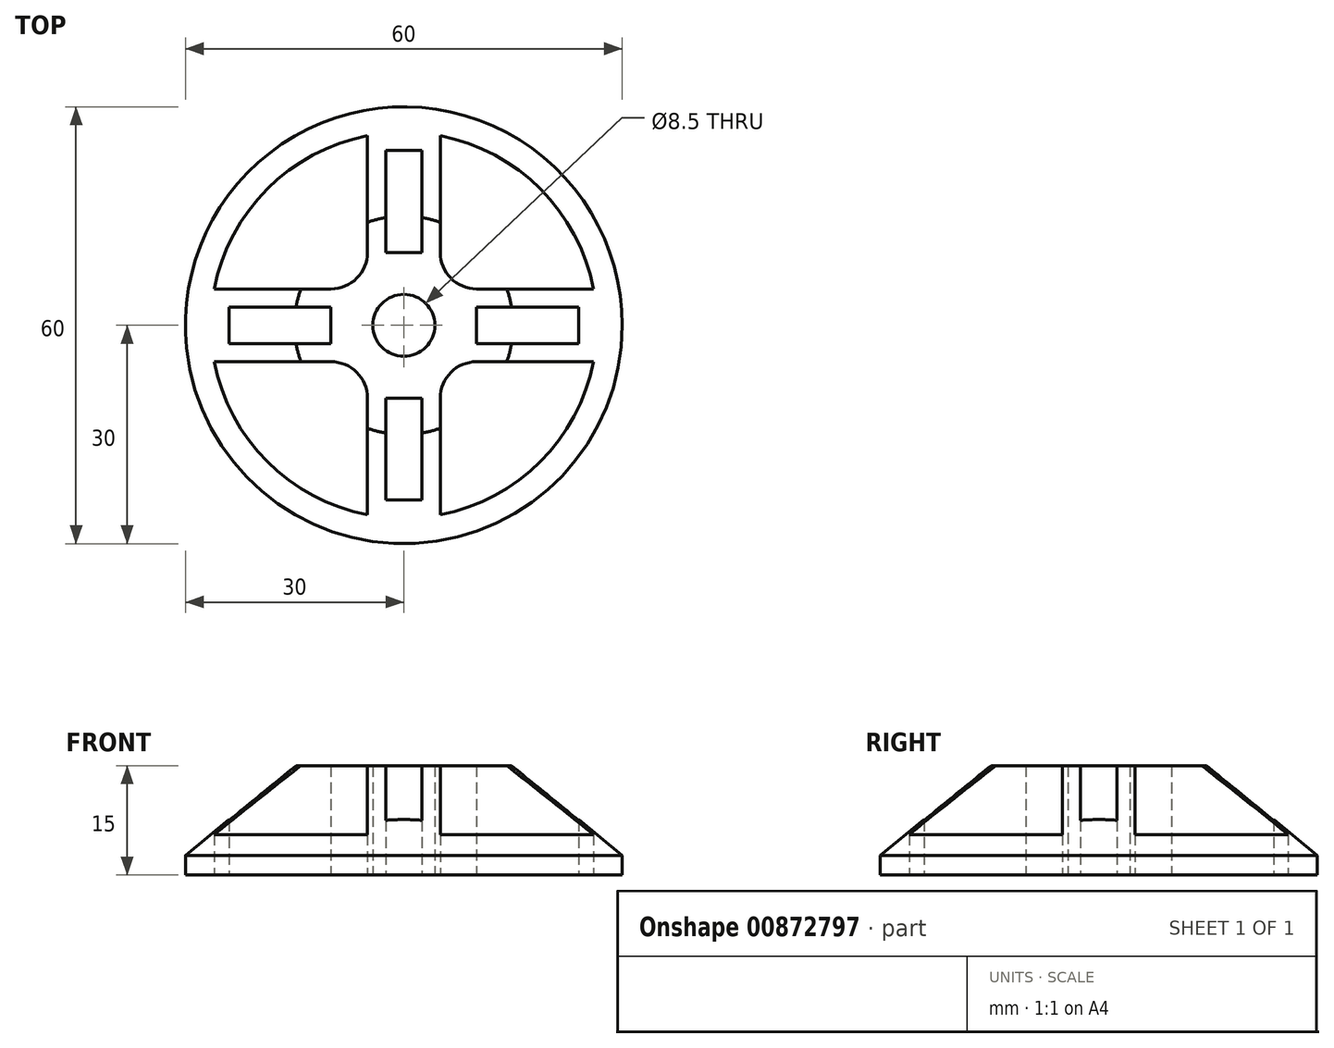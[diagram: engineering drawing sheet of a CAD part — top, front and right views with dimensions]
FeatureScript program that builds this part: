
annotation { "Feature Type Name" : "Feature", "Feature Type Description" : "" }
export const myFeature = defineFeature(function(context is Context, id is Id, definition is map)
    precondition{}
    {
        {
            assignVariable(context, id + "F0", {"name" : "Alto", "anyValue" : 15});
        }
        {
            var Q0;
            Q0=qCreatedBy(makeId("Top.planeOp"),FACE);
            var sketch = newSketch(context, id + "F1", { "sketchPlane" : qUnion([Q0])});
            skCircle(sketch, "E0", {"center": v(0, 0) * mm, "radius": 4.25 * mm});
            skCircle(sketch, "E1", {"center": v(0, 0) * mm, "radius": 30 * mm});
            skCircle(sketch, "E2", {"center": v(0, 0) * mm, "radius": 26.5 * mm});
            skLineSegment(sketch, "E3.bottom", {"start": v(-5, 42.51) * mm, "end": v(5, 42.51) * mm});
            skLineSegment(sketch, "E3.top", {"start": v(-5, -42.51) * mm, "end": v(5, -42.51) * mm});
            skLineSegment(sketch, "E3.left", {"start": v(-5, 42.51) * mm, "end": v(-5, -42.51) * mm});
            skLineSegment(sketch, "E3.right", {"start": v(5, 42.51) * mm, "end": v(5, -42.51) * mm});
            skLineSegment(sketch, "E4.bottom", {"start": v(-44.3, -5) * mm, "end": v(44.3, -5) * mm});
            skLineSegment(sketch, "E4.top", {"start": v(-44.3, 5) * mm, "end": v(44.3, 5) * mm});
            skLineSegment(sketch, "E4.left", {"start": v(-44.3, -5) * mm, "end": v(-44.3, 5) * mm});
            skLineSegment(sketch, "E4.right", {"start": v(44.3, -5) * mm, "end": v(44.3, 5) * mm});
            skLineSegment(sketch, "E5.bottom", {"start": v(10, -10) * mm, "end": v(-10, -10) * mm});
            skLineSegment(sketch, "E5.top", {"start": v(10, 10) * mm, "end": v(-10, 10) * mm});
            skLineSegment(sketch, "E5.left", {"start": v(10, -10) * mm, "end": v(10, 10) * mm});
            skLineSegment(sketch, "E5.right", {"start": v(-10, -10) * mm, "end": v(-10, 10) * mm});
            skLineSegment(sketch, "E6.bottom", {"start": v(24, -2.5) * mm, "end": v(-24, -2.5) * mm});
            skLineSegment(sketch, "E6.top", {"start": v(24, 2.5) * mm, "end": v(-24, 2.5) * mm});
            skLineSegment(sketch, "E6.left", {"start": v(24, -2.5) * mm, "end": v(24, 2.5) * mm});
            skLineSegment(sketch, "E6.right", {"start": v(-24, -2.5) * mm, "end": v(-24, 2.5) * mm});
            skLineSegment(sketch, "E7.bottom", {"start": v(-2.5, 24) * mm, "end": v(2.5, 24) * mm});
            skLineSegment(sketch, "E7.top", {"start": v(-2.5, -24) * mm, "end": v(2.5, -24) * mm});
            skLineSegment(sketch, "E7.left", {"start": v(-2.5, 24) * mm, "end": v(-2.5, -24) * mm});
            skLineSegment(sketch, "E7.right", {"start": v(2.5, 24) * mm, "end": v(2.5, -24) * mm});
            skSolve(sketch);
        }
        {
            var Q0;
            {var subQ0=sQuery(id+"F1.wireOp",EDGE,"E3.left");var subQ1=sQuery(id+"F1.wireOp",EDGE,"E1");var subQ2=makeQuery(id+"F1.imprint","INTERSECT",VERTEX,{"disambiguationData":[OD(0.0)],"derivedFrom":[subQ1,subQ0]});Q0=makeQuery(id+"F1.imprint","IMPRINT",FACE,{"disambiguationData":[TD([[makeQuery(id+"F1.imprint","IMPRINT",EDGE,{"disambiguationData":[TD([[subQ2,-1.0]])],"derivedFrom":subQ1}),1.0]])]});}
            var Q1;
            {var subQ0=sQuery(id+"F1.wireOp",EDGE,"E4.top");var subQ1=sQuery(id+"F1.wireOp",EDGE,"E1");var subQ2=makeQuery(id+"F1.imprint","INTERSECT",VERTEX,{"disambiguationData":[OD(1.0)],"derivedFrom":[subQ1,subQ0]});Q1=makeQuery(id+"F1.imprint","IMPRINT",FACE,{"disambiguationData":[TD([[makeQuery(id+"F1.imprint","IMPRINT",EDGE,{"disambiguationData":[TD([[subQ2,-1.0]])],"derivedFrom":subQ1}),1.0]])]});}
            var Q2;
            {var subQ0=sQuery(id+"F1.wireOp",EDGE,"E4.bottom");var subQ1=sQuery(id+"F1.wireOp",EDGE,"E1");var subQ2=makeQuery(id+"F1.imprint","INTERSECT",VERTEX,{"disambiguationData":[OD(0.0)],"derivedFrom":[subQ1,subQ0]});Q2=makeQuery(id+"F1.imprint","IMPRINT",FACE,{"disambiguationData":[TD([[makeQuery(id+"F1.imprint","IMPRINT",EDGE,{"disambiguationData":[TD([[subQ2,-1.0]])],"derivedFrom":subQ1}),1.0]])]});}
            var Q3;
            {var subQ0=sQuery(id+"F1.wireOp",EDGE,"E4.top");var subQ1=sQuery(id+"F1.wireOp",EDGE,"E2");var subQ2=makeQuery(id+"F1.imprint","INTERSECT",VERTEX,{"disambiguationData":[OD(1.0)],"derivedFrom":[subQ1,subQ0]});Q3=makeQuery(id+"F1.imprint","IMPRINT",FACE,{"disambiguationData":[TD([[makeQuery(id+"F1.imprint","IMPRINT",EDGE,{"disambiguationData":[TD([[subQ2,-1.0]])],"derivedFrom":subQ1}),1.0]])]});}
            var Q4;
            {var subQ0=sQuery(id+"F1.wireOp",EDGE,"E3.left");var subQ1=sQuery(id+"F1.wireOp",EDGE,"E2");var subQ2=makeQuery(id+"F1.imprint","INTERSECT",VERTEX,{"disambiguationData":[OD(1.0)],"derivedFrom":[subQ1,subQ0]});Q4=makeQuery(id+"F1.imprint","IMPRINT",FACE,{"disambiguationData":[TD([[makeQuery(id+"F1.imprint","IMPRINT",EDGE,{"disambiguationData":[TD([[subQ2,-1.0]])],"derivedFrom":subQ1}),1.0]])]});}
            var Q5;
            {var subQ0=sQuery(id+"F1.wireOp",EDGE,"E4.top");var subQ1=sQuery(id+"F1.wireOp",EDGE,"E2");var subQ2=makeQuery(id+"F1.imprint","INTERSECT",VERTEX,{"disambiguationData":[OD(0.0)],"derivedFrom":[subQ1,subQ0]});Q5=makeQuery(id+"F1.imprint","IMPRINT",FACE,{"disambiguationData":[TD([[makeQuery(id+"F1.imprint","IMPRINT",EDGE,{"disambiguationData":[TD([[subQ2,1.0]])],"derivedFrom":subQ1}),1.0]])]});}
            var Q6;
            {var subQ0=sQuery(id+"F1.wireOp",EDGE,"E3.right");var subQ1=sQuery(id+"F1.wireOp",EDGE,"E2");var subQ2=makeQuery(id+"F1.imprint","INTERSECT",VERTEX,{"disambiguationData":[OD(0.0)],"derivedFrom":[subQ1,subQ0]});Q6=makeQuery(id+"F1.imprint","IMPRINT",FACE,{"disambiguationData":[TD([[makeQuery(id+"F1.imprint","IMPRINT",EDGE,{"disambiguationData":[TD([[subQ2,-1.0]])],"derivedFrom":subQ1}),1.0]])]});}
            var Q7;
            {var subQ0=sQuery(id+"F1.wireOp",EDGE,"E3.right");var subQ1=sQuery(id+"F1.wireOp",EDGE,"E1");var subQ2=makeQuery(id+"F1.imprint","INTERSECT",VERTEX,{"disambiguationData":[OD(0.0)],"derivedFrom":[subQ1,subQ0]});Q7=makeQuery(id+"F1.imprint","IMPRINT",FACE,{"disambiguationData":[TD([[makeQuery(id+"F1.imprint","IMPRINT",EDGE,{"disambiguationData":[TD([[subQ2,1.0]])],"derivedFrom":subQ1}),1.0]])]});}
            var Q8;
            {var subQ0=sQuery(id+"F1.wireOp",EDGE,"E3.right");var subQ1=sQuery(id+"F1.wireOp",EDGE,"E1");var subQ2=makeQuery(id+"F1.imprint","INTERSECT",VERTEX,{"disambiguationData":[OD(0.0)],"derivedFrom":[subQ1,subQ0]});Q8=makeQuery(id+"F1.imprint","IMPRINT",FACE,{"disambiguationData":[TD([[makeQuery(id+"F1.imprint","IMPRINT",EDGE,{"disambiguationData":[TD([[subQ2,-1.0]])],"derivedFrom":subQ1}),1.0]])]});}
            var Q9;
            {var subQ0=sQuery(id+"F1.wireOp",EDGE,"E4.top");var subQ1=sQuery(id+"F1.wireOp",EDGE,"E1");var subQ2=makeQuery(id+"F1.imprint","INTERSECT",VERTEX,{"disambiguationData":[OD(0.0)],"derivedFrom":[subQ1,subQ0]});Q9=makeQuery(id+"F1.imprint","IMPRINT",FACE,{"disambiguationData":[TD([[makeQuery(id+"F1.imprint","IMPRINT",EDGE,{"disambiguationData":[TD([[subQ2,1.0]])],"derivedFrom":subQ1}),1.0]])]});}
            var Q10;
            Q10=makeQuery(id+"F1.imprint","IMPRINT",FACE,{"disambiguationData":[TD([[makeQuery(id+"F1.imprint","IMPRINT",EDGE,{"derivedFrom":sQuery(id+"F1.wireOp",EDGE,"E0")}),-1.0]])]});
            var Q11;
            {var subQ0=sQuery(id+"F1.wireOp",EDGE,"E3.right");var subQ1=sQuery(id+"F1.wireOp",EDGE,"E1");var subQ2=makeQuery(id+"F1.imprint","INTERSECT",VERTEX,{"disambiguationData":[OD(1.0)],"derivedFrom":[subQ1,subQ0]});Q11=makeQuery(id+"F1.imprint","IMPRINT",FACE,{"disambiguationData":[TD([[makeQuery(id+"F1.imprint","IMPRINT",EDGE,{"disambiguationData":[TD([[subQ2,-1.0]])],"derivedFrom":subQ1}),1.0]])]});}
            var Q12;
            {var subQ0=sQuery(id+"F1.wireOp",EDGE,"E3.left");var subQ1=sQuery(id+"F1.wireOp",EDGE,"E1");var subQ2=makeQuery(id+"F1.imprint","INTERSECT",VERTEX,{"disambiguationData":[OD(1.0)],"derivedFrom":[subQ1,subQ0]});Q12=makeQuery(id+"F1.imprint","IMPRINT",FACE,{"disambiguationData":[TD([[makeQuery(id+"F1.imprint","IMPRINT",EDGE,{"disambiguationData":[TD([[subQ2,-1.0]])],"derivedFrom":subQ1}),1.0]])]});}
            var Q13;
            {var subQ0=sQuery(id+"F1.wireOp",EDGE,"E4.top");var subQ1=sQuery(id+"F1.wireOp",EDGE,"E3.left");var subQ2=makeQuery(id+"F1.imprint","INTERSECT",VERTEX,{"derivedFrom":[subQ1,subQ0]});Q13=makeQuery(id+"F1.imprint","IMPRINT",FACE,{"disambiguationData":[TD([[makeQuery(id+"F1.imprint","IMPRINT",EDGE,{"disambiguationData":[TD([[subQ2,-1.0]])],"derivedFrom":subQ1}),-1.0]])]});}
            var Q14;
            {var subQ3=sQuery(id+"F1.wireOp",EDGE,"E7.left");var subQ7=sQuery(id+"F1.wireOp",EDGE,"E0");var subQ9=makeQuery(id+"F1.imprint","INTERSECT",VERTEX,{"disambiguationData":[OD(0.0)],"derivedFrom":[subQ7,subQ3]});Q14=makeQuery(id+"F1.imprint","IMPRINT",FACE,{"disambiguationData":[TD([[makeQuery(id+"F1.imprint","IMPRINT",EDGE,{"disambiguationData":[TD([[subQ9,-1.0]])],"derivedFrom":subQ7}),-1.0]])]});}
            var Q15;
            {var subQ1=sQuery(id+"F1.wireOp",EDGE,"E0");var subQ5=sQuery(id+"F1.wireOp",EDGE,"E7.right");var subQ6=makeQuery(id+"F1.imprint","INTERSECT",VERTEX,{"disambiguationData":[OD(0.0)],"derivedFrom":[subQ1,subQ5]});Q15=makeQuery(id+"F1.imprint","IMPRINT",FACE,{"disambiguationData":[TD([[makeQuery(id+"F1.imprint","IMPRINT",EDGE,{"disambiguationData":[TD([[subQ6,1.0]])],"derivedFrom":subQ1}),-1.0]])]});}
            var Q16;
            {var subQ0=sQuery(id+"F1.wireOp",EDGE,"E4.top");var subQ1=sQuery(id+"F1.wireOp",EDGE,"E3.right");var subQ2=makeQuery(id+"F1.imprint","INTERSECT",VERTEX,{"derivedFrom":[subQ1,subQ0]});Q16=makeQuery(id+"F1.imprint","IMPRINT",FACE,{"disambiguationData":[TD([[makeQuery(id+"F1.imprint","IMPRINT",EDGE,{"disambiguationData":[TD([[subQ2,-1.0]])],"derivedFrom":subQ1}),1.0]])]});}
            var Q17;
            {var subQ0=sQuery(id+"F1.wireOp",EDGE,"E4.bottom");var subQ1=sQuery(id+"F1.wireOp",EDGE,"E3.right");var subQ2=makeQuery(id+"F1.imprint","INTERSECT",VERTEX,{"derivedFrom":[subQ1,subQ0]});Q17=makeQuery(id+"F1.imprint","IMPRINT",FACE,{"disambiguationData":[TD([[makeQuery(id+"F1.imprint","IMPRINT",EDGE,{"disambiguationData":[TD([[subQ2,-1.0]])],"derivedFrom":subQ1}),-1.0]])]});}
            var Q18;
            {var subQ0=sQuery(id+"F1.wireOp",EDGE,"E7.left");var subQ1=sQuery(id+"F1.wireOp",EDGE,"E4.bottom");var subQ2=makeQuery(id+"F1.imprint","INTERSECT",VERTEX,{"derivedFrom":[subQ1,subQ0]});Q18=makeQuery(id+"F1.imprint","IMPRINT",FACE,{"disambiguationData":[TD([[makeQuery(id+"F1.imprint","IMPRINT",EDGE,{"disambiguationData":[TD([[subQ2,-1.0]])],"derivedFrom":subQ1}),-1.0]])]});}
            var Q19;
            {var subQ0=sQuery(id+"F1.wireOp",EDGE,"E4.bottom");var subQ1=sQuery(id+"F1.wireOp",EDGE,"E3.left");var subQ2=makeQuery(id+"F1.imprint","INTERSECT",VERTEX,{"derivedFrom":[subQ1,subQ0]});Q19=makeQuery(id+"F1.imprint","IMPRINT",FACE,{"disambiguationData":[TD([[makeQuery(id+"F1.imprint","IMPRINT",EDGE,{"disambiguationData":[TD([[subQ2,-1.0]])],"derivedFrom":subQ1}),1.0]])]});}
            var Q20;
            {var subQ1=sQuery(id+"F1.wireOp",EDGE,"E0");var subQ5=sQuery(id+"F1.wireOp",EDGE,"E7.right");var subQ6=makeQuery(id+"F1.imprint","INTERSECT",VERTEX,{"disambiguationData":[OD(1.0)],"derivedFrom":[subQ1,subQ5]});Q20=makeQuery(id+"F1.imprint","IMPRINT",FACE,{"disambiguationData":[TD([[makeQuery(id+"F1.imprint","IMPRINT",EDGE,{"disambiguationData":[TD([[subQ6,-1.0]])],"derivedFrom":subQ1}),-1.0]])]});}
            var Q21;
            {var subQ0=sQuery(id+"F1.wireOp",EDGE,"E6.bottom");var subQ1=sQuery(id+"F1.wireOp",EDGE,"E0");var subQ2=makeQuery(id+"F1.imprint","INTERSECT",VERTEX,{"disambiguationData":[OD(0.0)],"derivedFrom":[subQ1,subQ0]});Q21=makeQuery(id+"F1.imprint","IMPRINT",FACE,{"disambiguationData":[TD([[makeQuery(id+"F1.imprint","IMPRINT",EDGE,{"disambiguationData":[TD([[subQ2,-1.0]])],"derivedFrom":subQ1}),-1.0]])]});}
            var Q22;
            {var subQ0=sQuery(id+"F1.wireOp",EDGE,"E6.bottom");var subQ1=sQuery(id+"F1.wireOp",EDGE,"E3.left");var subQ2=makeQuery(id+"F1.imprint","INTERSECT",VERTEX,{"derivedFrom":[subQ1,subQ0]});Q22=makeQuery(id+"F1.imprint","IMPRINT",FACE,{"disambiguationData":[TD([[makeQuery(id+"F1.imprint","IMPRINT",EDGE,{"disambiguationData":[TD([[subQ2,-1.0]])],"derivedFrom":subQ1}),-1.0]])]});}
            var Q23;
            {var subQ0=sQuery(id+"F1.wireOp",EDGE,"E6.bottom");var subQ1=sQuery(id+"F1.wireOp",EDGE,"E3.right");var subQ2=makeQuery(id+"F1.imprint","INTERSECT",VERTEX,{"derivedFrom":[subQ1,subQ0]});Q23=makeQuery(id+"F1.imprint","IMPRINT",FACE,{"disambiguationData":[TD([[makeQuery(id+"F1.imprint","IMPRINT",EDGE,{"disambiguationData":[TD([[subQ2,-1.0]])],"derivedFrom":subQ1}),1.0]])]});}
            var Q24;
            {var subQ0=sQuery(id+"F1.wireOp",EDGE,"E5.top");var subQ1=sQuery(id+"F1.wireOp",EDGE,"E3.right");var subQ2=makeQuery(id+"F1.imprint","INTERSECT",VERTEX,{"derivedFrom":[subQ1,subQ0]});Q24=makeQuery(id+"F1.imprint","IMPRINT",FACE,{"disambiguationData":[TD([[makeQuery(id+"F1.imprint","IMPRINT",EDGE,{"disambiguationData":[TD([[subQ2,-1.0]])],"derivedFrom":subQ1}),-1.0]])]});}
            var Q25;
            {var subQ0=sQuery(id+"F1.wireOp",EDGE,"E7.left");var subQ1=sQuery(id+"F1.wireOp",EDGE,"E4.top");var subQ2=makeQuery(id+"F1.imprint","INTERSECT",VERTEX,{"derivedFrom":[subQ1,subQ0]});Q25=makeQuery(id+"F1.imprint","IMPRINT",FACE,{"disambiguationData":[TD([[makeQuery(id+"F1.imprint","IMPRINT",EDGE,{"disambiguationData":[TD([[subQ2,-1.0]])],"derivedFrom":subQ1}),1.0]])]});}
            var Q26;
            {var subQ0=sQuery(id+"F1.wireOp",EDGE,"E6.top");var subQ1=sQuery(id+"F1.wireOp",EDGE,"E3.left");var subQ2=makeQuery(id+"F1.imprint","INTERSECT",VERTEX,{"derivedFrom":[subQ1,subQ0]});Q26=makeQuery(id+"F1.imprint","IMPRINT",FACE,{"disambiguationData":[TD([[makeQuery(id+"F1.imprint","IMPRINT",EDGE,{"disambiguationData":[TD([[subQ2,-1.0]])],"derivedFrom":subQ1}),-1.0]])]});}
            var Q27;
            {var subQ0=sQuery(id+"F1.wireOp",EDGE,"E6.top");var subQ1=sQuery(id+"F1.wireOp",EDGE,"E3.right");var subQ2=makeQuery(id+"F1.imprint","INTERSECT",VERTEX,{"derivedFrom":[subQ1,subQ0]});Q27=makeQuery(id+"F1.imprint","IMPRINT",FACE,{"disambiguationData":[TD([[makeQuery(id+"F1.imprint","IMPRINT",EDGE,{"disambiguationData":[TD([[subQ2,-1.0]])],"derivedFrom":subQ1}),1.0]])]});}
            var Q28;
            {var subQ0=sQuery(id+"F1.wireOp",EDGE,"E5.top");var subQ1=sQuery(id+"F1.wireOp",EDGE,"E3.left");var subQ2=makeQuery(id+"F1.imprint","INTERSECT",VERTEX,{"derivedFrom":[subQ1,subQ0]});Q28=makeQuery(id+"F1.imprint","IMPRINT",FACE,{"disambiguationData":[TD([[makeQuery(id+"F1.imprint","IMPRINT",EDGE,{"disambiguationData":[TD([[subQ2,-1.0]])],"derivedFrom":subQ1}),1.0]])]});}
            extrude(context, id + "F2", {"entities" : qUnion([Q0, Q1, Q2, Q3, Q4, Q5, Q6, Q7, Q8, Q9, Q10, Q11, Q12, Q13, Q14, Q15, Q16, Q17, Q18, Q19, Q20, Q21, Q22, Q23, Q24, Q25, Q26, Q27, Q28]), "depth" : (getVariable(context, 'Alto')) * mm, "offsetDistance" : 25 * mm});
        }
        {
            var Q0;
            Q0=qCreatedBy(makeId("Front.planeOp"),FACE);
            var sketch = newSketch(context, id + "F3", { "sketchPlane" : qUnion([Q0])});
            skLineSegment(sketch, "E8", {"start": v(0, 0) * mm, "end": v(-30, 0) * mm});
            skLineSegment(sketch, "E9", {"start": v(-30, 0) * mm, "end": v(-30, 2.7) * mm});
            skLineSegment(sketch, "E10", {"start": v(0, 0) * mm, "end": v(0, 15) * mm});
            skLineSegment(sketch, "E11", {"start": v(0, 15) * mm, "end": v(-15, 15) * mm});
            skLineSegment(sketch, "E12", {"start": v(-15, 15) * mm, "end": v(-30, 2.7) * mm});
            skLineSegment(sketch, "E13", {"start": v(-15, 15) * mm, "end": v(-30, 15) * mm});
            skLineSegment(sketch, "E14", {"start": v(-30, 15) * mm, "end": v(-30, 2.7) * mm});
            skSolve(sketch);
        }
        {
            var Q0;
            Q0=makeQuery(id+"F3.imprint","IMPRINT",FACE,{"disambiguationData":[TD([[makeQuery(id+"F3.imprint","IMPRINT",EDGE,{"derivedFrom":sQuery(id+"F3.wireOp",EDGE,"E12")}),-1.0]])]});
            var Q1;
            Q1=sQuery(id+"F3.wireOp",EDGE,"E10");
            revolve(context, id + "F4", {"operationType" : NewBodyOperationType.REMOVE, "surfaceOperationType" : NewSurfaceOperationType.NEW, "entities" : qUnion([Q0]), "axis" : qUnion([Q1]), "revolveType" : RevolveType.FULL, "oppositeDirection" : true});
        }
        {
            var Q0;
            Q0=makeQuery(id+"F2.opExtrude","SWEPT_EDGE",EDGE,{"disambiguationData":[OSD([sQuery(id+"F1.wireOp",EDGE,"E3.right"),sQuery(id+"F1.wireOp",EDGE,"E4.top")])]});
            var Q1;
            Q1=makeQuery(id+"F2.opExtrude","SWEPT_EDGE",EDGE,{"disambiguationData":[OSD([sQuery(id+"F1.wireOp",EDGE,"E3.right"),sQuery(id+"F1.wireOp",EDGE,"E4.bottom")])]});
            var Q2;
            Q2=makeQuery(id+"F2.opExtrude","SWEPT_EDGE",EDGE,{"disambiguationData":[OSD([sQuery(id+"F1.wireOp",EDGE,"E3.left"),sQuery(id+"F1.wireOp",EDGE,"E4.bottom")])]});
            var Q3;
            Q3=makeQuery(id+"F2.opExtrude","SWEPT_EDGE",EDGE,{"disambiguationData":[OSD([sQuery(id+"F1.wireOp",EDGE,"E3.left"),sQuery(id+"F1.wireOp",EDGE,"E4.top")])]});
            fillet(context, id + "F5", {"entities" : qUnion([Q0, Q1, Q2, Q3]), "radius" : 5 * mm, "tangentPropagation" : true, "allowEdgeOverflow" : false});
        }
    });
